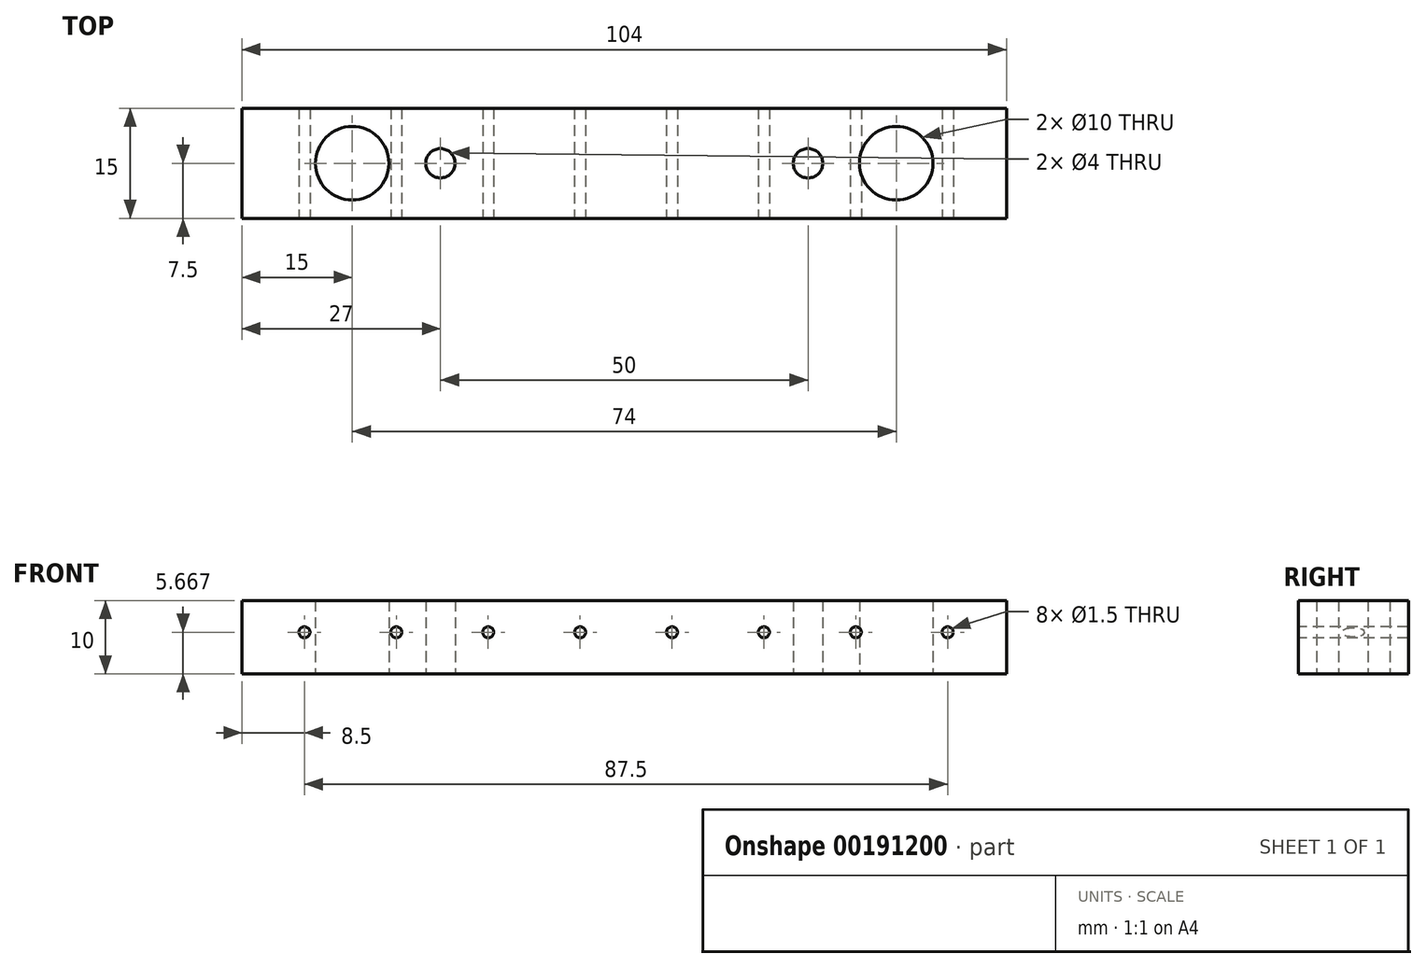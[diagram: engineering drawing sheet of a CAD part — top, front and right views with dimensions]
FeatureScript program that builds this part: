
annotation { "Feature Type Name" : "Feature", "Feature Type Description" : "" }
export const myFeature = defineFeature(function(context is Context, id is Id, definition is map)
    precondition{}
    {
        {
            var Q0;
            Q0=qCreatedBy(makeId("Top.planeOp"),FACE);
            var sketch = newSketch(context, id + "F0", { "sketchPlane" : qUnion([Q0])});
            skLineSegment(sketch, "E0.bottom", {"start": v(52, -7.5) * mm, "end": v(-52, -7.5) * mm});
            skLineSegment(sketch, "E0.top", {"start": v(52, 7.5) * mm, "end": v(-52, 7.5) * mm});
            skLineSegment(sketch, "E0.left", {"start": v(52, -7.5) * mm, "end": v(52, 7.5) * mm});
            skLineSegment(sketch, "E0.right", {"start": v(-52, -7.5) * mm, "end": v(-52, 7.5) * mm});
            skPoint(sketch, "E0.middle", {"position": v(0, 0) * mm});
            skCircle(sketch, "E1", {"center": v(-37, 0) * mm, "radius": 5 * mm});
            skPoint(sketch, "E2.centerSnap0", {"position": v(-52, 0) * mm});
            skCircle(sketch, "E3", {"center": v(37, 0) * mm, "radius": 5 * mm});
            skCircle(sketch, "E4", {"center": v(-25, 0) * mm, "radius": 2 * mm});
            skCircle(sketch, "E5", {"center": v(25, 0) * mm, "radius": 2 * mm});
            skSolve(sketch);
        }
        {
            var Q0;
            Q0 = qSketchRegion(id + "F0", true);
            extrude(context, id + "F1", {"entities" : qUnion([Q0]), "depth" : 10 * mm});
        }
        {
            var Q0;
            Q0=makeQuery(id+"F1.opExtrude","SWEPT_FACE",FACE,{"disambiguationData":[OSD([sQuery(id+"F0.wireOp",EDGE,"E0.bottom")])]});
            var sketch = newSketch(context, id + "F2", { "sketchPlane" : qUnion([Q0])});
            skCircle(sketch, "E6", {"center": v(-43.5, 5.67) * mm, "radius": 0.75 * mm});
            skCircle(sketch, "E7.1.0.0", {"center": v(-31, 5.67) * mm, "radius": 0.75 * mm});
            skCircle(sketch, "E7.2.0.0", {"center": v(-18.5, 5.67) * mm, "radius": 0.75 * mm});
            skCircle(sketch, "E7.3.0.0", {"center": v(-6, 5.67) * mm, "radius": 0.75 * mm});
            skCircle(sketch, "E7.4.0.0", {"center": v(6.5, 5.67) * mm, "radius": 0.75 * mm});
            skCircle(sketch, "E7.5.0.0", {"center": v(19, 5.67) * mm, "radius": 0.75 * mm});
            skCircle(sketch, "E7.6.0.0", {"center": v(31.5, 5.67) * mm, "radius": 0.75 * mm});
            skCircle(sketch, "E7.7.0.0", {"center": v(44, 5.67) * mm, "radius": 0.75 * mm});
            skLineSegment(sketch, "E7.direction1", {"start": v(-43.5, 5.67) * mm, "end": v(-31, 5.67) * mm, "construction": true});
            skSolve(sketch);
        }
        {
            var Q0;
            Q0 = qSketchRegion(id + "F2", true);
            extrude(context, id + "F3", {"entities" : qUnion([Q0]), "operationType" : NewBodyOperationType.REMOVE, "oppositeDirection" : true, "depth" : 25 * mm});
        }
    });
